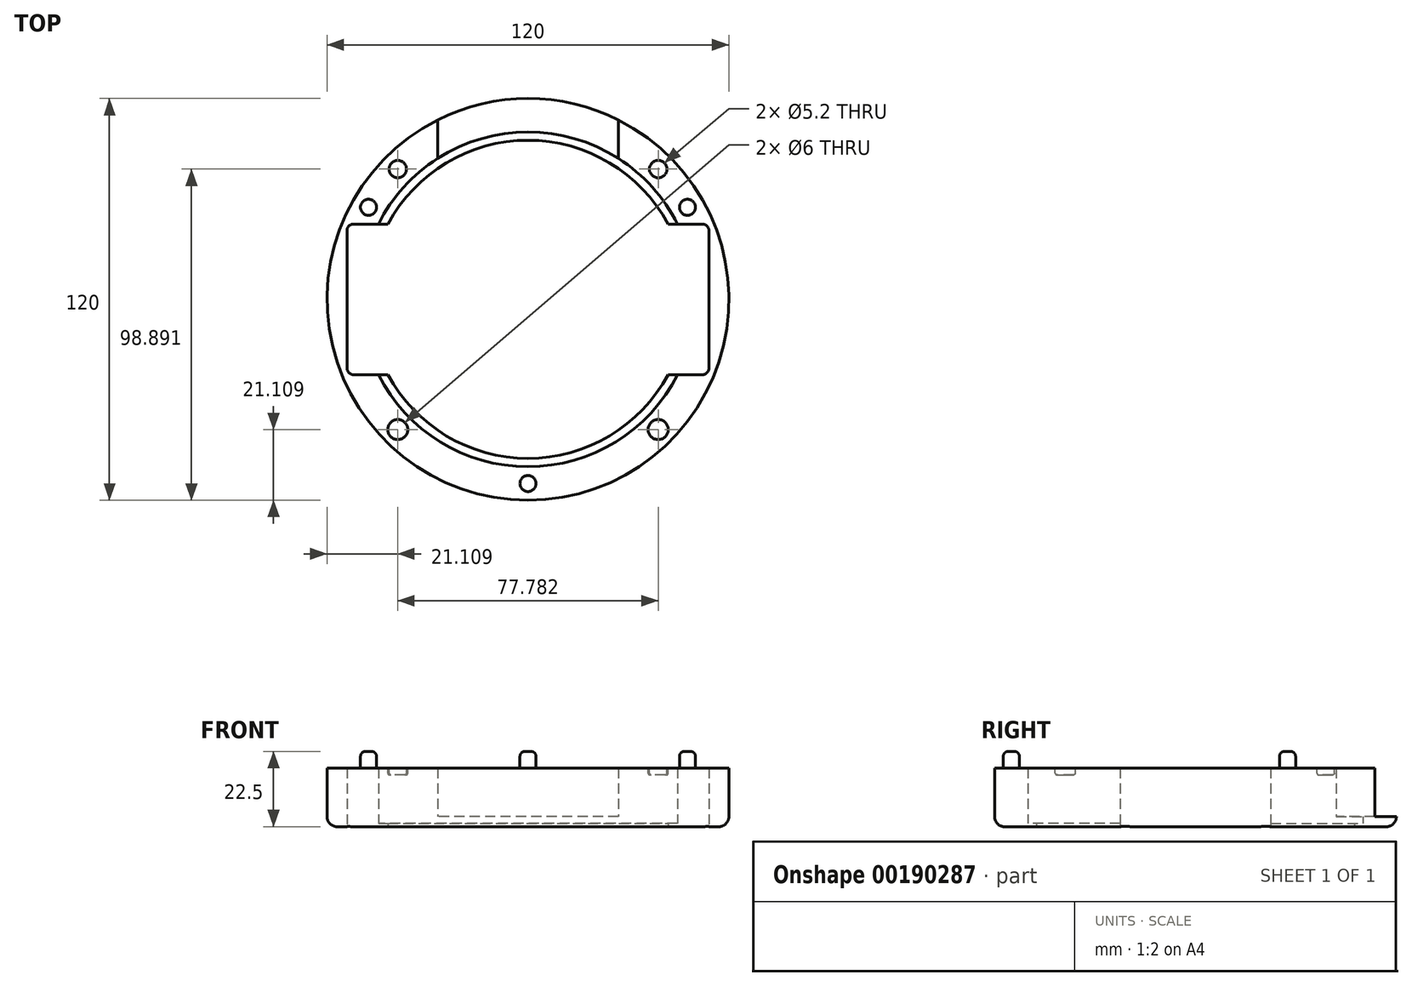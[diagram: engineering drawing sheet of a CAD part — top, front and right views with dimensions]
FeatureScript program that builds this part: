
annotation { "Feature Type Name" : "Feature", "Feature Type Description" : "" }
export const myFeature = defineFeature(function(context is Context, id is Id, definition is map)
    precondition{}
    {
        {
            var Q0;
            Q0=qCreatedBy(makeId("Top.planeOp"),FACE);
            var sketch = newSketch(context, id + "F0", { "sketchPlane" : qUnion([Q0])});
            skCircle(sketch, "E0", {"center": v(0, 0) * mm, "radius": 60 * mm});
            skLineSegment(sketch, "E1", {"start": v(0, 50) * mm, "end": v(0, 50) * mm});
            skArc(sketch, "E2", {"start": v(-44.65, -22.5) * mm, "mid": v(0, -50) * mm, "end": v(44.65, -22.5) * mm});
            skArc(sketch, "E3", {"start": v(-41.83, -22.5) * mm, "mid": v(0, -47.5) * mm, "end": v(41.83, -22.5) * mm});
            skPoint(sketch, "E4.orphan", {"position": v(55.62, -22.5) * mm});
            skLineSegment(sketch, "E5", {"start": v(-44.65, 22.5) * mm, "end": v(-41.83, 22.5) * mm});
            skLineSegment(sketch, "E6", {"start": v(44.65, 22.5) * mm, "end": v(41.83, 22.5) * mm});
            skLineSegment(sketch, "E7.MirrorCS", {"start": v(-44.65, -22.5) * mm, "end": v(-41.83, -22.5) * mm});
            skLineSegment(sketch, "E8.MirrorCS", {"start": v(44.65, -22.5) * mm, "end": v(41.83, -22.5) * mm});
            skArc(sketch, "E9.trimOffspring", {"start": v(41.83, 22.5) * mm, "mid": v(0, 47.5) * mm, "end": v(-41.83, 22.5) * mm});
            skArc(sketch, "E10.trimOffspring", {"start": v(44.65, 22.5) * mm, "mid": v(0, 50) * mm, "end": v(-44.65, 22.5) * mm});
            skLineSegment(sketch, "E11", {"start": v(-27, 53.58) * mm, "end": v(-27, 42.08) * mm});
            skLineSegment(sketch, "E12", {"start": v(27, 53.58) * mm, "end": v(27, 42.08) * mm});
            skLineSegment(sketch, "E13", {"start": v(-27, 53.58) * mm, "end": v(27, 53.58) * mm, "construction": true});
            skLineSegment(sketch, "E14", {"start": v(-44.65, 22.5) * mm, "end": v(-54.05, 22.5) * mm});
            skLineSegment(sketch, "E15", {"start": v(-54.05, 22.5) * mm, "end": v(-54.05, -22.5) * mm});
            skLineSegment(sketch, "E16", {"start": v(-54.05, -22.5) * mm, "end": v(-44.65, -22.5) * mm});
            skLineSegment(sketch, "E17", {"start": v(0, 60) * mm, "end": v(0, -60) * mm, "construction": true});
            skPoint(sketch, "E17.startSnap0", {"position": v(0, 53.58) * mm});
            skPoint(sketch, "E17.endSnap0", {"position": v(0, 47.5) * mm});
            skLineSegment(sketch, "E18.MirrorCS", {"start": v(54.05, 22.5) * mm, "end": v(54.05, -22.5) * mm});
            skLineSegment(sketch, "E19.MirrorCS", {"start": v(44.65, 22.5) * mm, "end": v(54.05, 22.5) * mm});
            skLineSegment(sketch, "E20.MirrorCS", {"start": v(54.05, -22.5) * mm, "end": v(44.65, -22.5) * mm});
            skSolve(sketch);
        }
        {
            var Q0;
            Q0=makeQuery(id+"F0.imprint","IMPRINT",FACE,{"disambiguationData":[TD([[makeQuery(id+"F0.imprint","IMPRINT",EDGE,{"derivedFrom":sQuery(id+"F0.wireOp",EDGE,"E2")}),-1.0]])]});
            extrude(context, id + "F1", {"entities" : qUnion([Q0]), "depth" : 17.5 * mm});
        }
        {
            var Q0;
            Q0=makeQuery(id+"F1.opExtrude","CAP_FACE",FACE,{"disambiguationData":[OSD([sQuery(id+"F0.wireOp",EDGE,"E0"),sQuery(id+"F0.wireOp",EDGE,"E1")])],"isStart":false});
            var sketch = newSketch(context, id + "F2", { "sketchPlane" : qUnion([Q0])});
            skPoint(sketch, "E21.middle", {"position": v(0, 0) * mm});
            skCircle(sketch, "E22", {"center": v(-38.9, 38.9) * mm, "radius": 2.6 * mm});
            skCircle(sketch, "E23", {"center": v(-38.9, -38.9) * mm, "radius": 3 * mm});
            skCircle(sketch, "E24", {"center": v(38.9, -38.9) * mm, "radius": 3 * mm});
            skCircle(sketch, "E25", {"center": v(38.9, 38.9) * mm, "radius": 2.6 * mm});
            skCircle(sketch, "E26", {"center": v(0, -55) * mm, "radius": 2.4 * mm});
            skCircle(sketch, "E27.1.0", {"center": v(47.63, 27.5) * mm, "radius": 2.4 * mm});
            skCircle(sketch, "E27.2.0", {"center": v(-47.63, 27.5) * mm, "radius": 2.4 * mm});
            skSolve(sketch);
        }
        {
            var Q0;
            Q0=makeQuery(id+"F2.imprint","IMPRINT",FACE,{"disambiguationData":[TD([[makeQuery(id+"F2.imprint","IMPRINT",EDGE,{"derivedFrom":sQuery(id+"F2.wireOp",EDGE,"E22")}),1.0]])]});
            var Q1;
            Q1=makeQuery(id+"F2.imprint","IMPRINT",FACE,{"disambiguationData":[TD([[makeQuery(id+"F2.imprint","IMPRINT",EDGE,{"derivedFrom":sQuery(id+"F2.wireOp",EDGE,"E25")}),1.0]])]});
            var Q2;
            Q2=makeQuery(id+"F2.imprint","IMPRINT",FACE,{"disambiguationData":[TD([[makeQuery(id+"F2.imprint","IMPRINT",EDGE,{"derivedFrom":sQuery(id+"F2.wireOp",EDGE,"E24")}),1.0]])]});
            var Q3;
            Q3=makeQuery(id+"F2.imprint","IMPRINT",FACE,{"disambiguationData":[TD([[makeQuery(id+"F2.imprint","IMPRINT",EDGE,{"derivedFrom":sQuery(id+"F2.wireOp",EDGE,"E23")}),1.0]])]});
            extrude(context, id + "F3", {"entities" : qUnion([Q0, Q1, Q2, Q3]), "operationType" : NewBodyOperationType.REMOVE, "oppositeDirection" : true, "depth" : 2 * mm});
        }
        {
            var Q0;
            Q0=makeQuery(id+"F2.imprint","IMPRINT",FACE,{"disambiguationData":[TD([[makeQuery(id+"F2.imprint","IMPRINT",EDGE,{"derivedFrom":sQuery(id+"F2.wireOp",EDGE,"E26")}),1.0]])]});
            var Q1;
            Q1=makeQuery(id+"F2.imprint","IMPRINT",FACE,{"disambiguationData":[TD([[makeQuery(id+"F2.imprint","IMPRINT",EDGE,{"derivedFrom":sQuery(id+"F2.wireOp",EDGE,"E27.1.0")}),1.0]])]});
            var Q2;
            Q2=makeQuery(id+"F2.imprint","IMPRINT",FACE,{"disambiguationData":[TD([[makeQuery(id+"F2.imprint","IMPRINT",EDGE,{"derivedFrom":sQuery(id+"F2.wireOp",EDGE,"E27.2.0")}),1.0]])]});
            var Q3;
            Q3=sQuery(id+"F2.wireOp",EDGE,"VWXdR3C8-mcWa-IJBR-1boV-t68bjsxYqndP");
            var Q4;
            Q4=sQuery(id+"F2.wireOp",EDGE,"uHltdg73-JYHf-iSAY-R7Fn-2nbyHwWvfhgZ");
            var Q5;
            Q5=sQuery(id+"F2.wireOp",EDGE,"R24LEf0a-MQ1t-eLEK-fKfR-x5qMptQUL0lt");
            extrude(context, id + "F4", {"entities" : qUnion([Q0, Q1, Q2]), "operationType" : NewBodyOperationType.ADD, "surfaceEntities" : qUnion([Q3, Q4, Q5]), "depth" : 5 * mm});
        }
        {
            var Q0;
            Q0=makeQuery(id+"F3.boolean.opBoolean","COPY",EDGE,{"derivedFrom":makeQuery(id+"F3.opExtrude","CAP_EDGE",EDGE,{"disambiguationData":[OSD([sQuery(id+"F2.wireOp",EDGE,"E24")])],"isStart":false})});
            var Q1;
            Q1=makeQuery(id+"F3.boolean.opBoolean","COPY",EDGE,{"derivedFrom":makeQuery(id+"F3.opExtrude","CAP_EDGE",EDGE,{"disambiguationData":[OSD([sQuery(id+"F2.wireOp",EDGE,"E23")])],"isStart":false})});
            var Q2;
            Q2=makeQuery(id+"F3.boolean.opBoolean","COPY",EDGE,{"derivedFrom":makeQuery(id+"F3.opExtrude","CAP_EDGE",EDGE,{"disambiguationData":[OSD([sQuery(id+"F2.wireOp",EDGE,"E22")])],"isStart":false})});
            var Q3;
            Q3=makeQuery(id+"F3.boolean.opBoolean","COPY",EDGE,{"derivedFrom":makeQuery(id+"F3.opExtrude","CAP_EDGE",EDGE,{"disambiguationData":[OSD([sQuery(id+"F2.wireOp",EDGE,"E25")])],"isStart":false})});
            fillet(context, id + "F5", {"entities" : qUnion([Q0, Q1, Q2, Q3]), "radius" : 0.5 * mm, "tangentPropagation" : true, "allowEdgeOverflow" : false});
        }
        {
            var Q0;
            Q0=makeQuery(id+"F4.opExtrude","CAP_EDGE",EDGE,{"disambiguationData":[OSD([sQuery(id+"F2.wireOp",EDGE,"E26")])],"isStart":false});
            var Q1;
            Q1=makeQuery(id+"F4.opExtrude","CAP_EDGE",EDGE,{"disambiguationData":[OSD([sQuery(id+"F2.wireOp",EDGE,"E27.2.0")])],"isStart":false});
            var Q2;
            Q2=makeQuery(id+"F4.opExtrude","CAP_EDGE",EDGE,{"disambiguationData":[OSD([sQuery(id+"F2.wireOp",EDGE,"E27.1.0")])],"isStart":false});
            var Q3;
            Q3=makeQuery(id+"FGFiXdv48eJCvJ8_2.boolean.opBoolean","COPY",EDGE,{"derivedFrom":makeQuery(id+"FGFiXdv48eJCvJ8_2.opExtrude","CAP_EDGE",EDGE,{"disambiguationData":[OSD([sQuery(id+"Fr2hoOnM7MHRwgI_2.wireOp",EDGE,"7669c31a-f0c1-4fce-9309-ce77d950d35b.0")])],"isStart":false})});
            var Q4;
            Q4=makeQuery(id+"FGFiXdv48eJCvJ8_2.boolean.opBoolean","COPY",EDGE,{"derivedFrom":makeQuery(id+"FGFiXdv48eJCvJ8_2.opExtrude","CAP_EDGE",EDGE,{"disambiguationData":[OSD([sQuery(id+"Fr2hoOnM7MHRwgI_2.wireOp",EDGE,"7669c31a-f0c1-4fce-9309-ce77d950d35b.1")])],"isStart":false})});
            var Q5;
            Q5=makeQuery(id+"FGFiXdv48eJCvJ8_2.boolean.opBoolean","COPY",EDGE,{"derivedFrom":makeQuery(id+"FGFiXdv48eJCvJ8_2.opExtrude","CAP_EDGE",EDGE,{"disambiguationData":[OSD([sQuery(id+"Fr2hoOnM7MHRwgI_2.wireOp",EDGE,"7669c31a-f0c1-4fce-9309-ce77d950d35b.2")])],"isStart":false})});
            fillet(context, id + "F6", {"entities" : qUnion([Q0, Q1, Q2, Q3, Q4, Q5]), "radius" : 1.5 * mm, "tangentPropagation" : true, "allowEdgeOverflow" : false});
        }
        {
            var Q0;
            Q0=makeQuery(id+"F1.opExtrude","SWEPT_BODY",BODY,{"disambiguationData":[OSD([sQuery(id+"F0.wireOp",EDGE,"E0"),sQuery(id+"F0.wireOp",EDGE,"E1"),sQuery(id+"F0.wireOp",EDGE,"Z948ch8O-qMHw-9Xcc-9FHW-eBQYffAlLzsf"),sQuery(id+"F0.wireOp",EDGE,"A77KNi0v-6heQ-Jye2-6KwH-JstxTwlQuu4X.top"),sQuery(id+"F0.wireOp",EDGE,"A77KNi0v-6heQ-Jye2-6KwH-JstxTwlQuu4X.left"),sQuery(id+"F0.wireOp",EDGE,"A77KNi0v-6heQ-Jye2-6KwH-JstxTwlQuu4X.right"),sQuery(id+"F0.wireOp",EDGE,"e3c13985-3201-4729-a912-cdfdbae41750.trimOffspring"),sQuery(id+"F0.wireOp",EDGE,"hgyFUOab-B19C-UYkE-toPB-BuUCfqlj2oRy.bottom")])]});
            transform(context, id + "F7", {"entities" : qUnion([Q0]), "transformType" : TransformType.TRANSLATION_3D, "dx" : 0 * mm, "dy" : 0 * mm, "dz" : 0 * mm, "makeCopy" : true});
        }
        {
            var Q0;
            Q0=makeQuery(id+"F7.opPattern","COPY",BODY,{"derivedFrom":makeQuery(id+"F1.opExtrude","SWEPT_BODY",BODY,{"disambiguationData":[OSD([sQuery(id+"F0.wireOp",EDGE,"E0"),sQuery(id+"F0.wireOp",EDGE,"E1"),sQuery(id+"F0.wireOp",EDGE,"Z948ch8O-qMHw-9Xcc-9FHW-eBQYffAlLzsf"),sQuery(id+"F0.wireOp",EDGE,"A77KNi0v-6heQ-Jye2-6KwH-JstxTwlQuu4X.top"),sQuery(id+"F0.wireOp",EDGE,"A77KNi0v-6heQ-Jye2-6KwH-JstxTwlQuu4X.left"),sQuery(id+"F0.wireOp",EDGE,"A77KNi0v-6heQ-Jye2-6KwH-JstxTwlQuu4X.right"),sQuery(id+"F0.wireOp",EDGE,"e3c13985-3201-4729-a912-cdfdbae41750.trimOffspring"),sQuery(id+"F0.wireOp",EDGE,"hgyFUOab-B19C-UYkE-toPB-BuUCfqlj2oRy.bottom")])]}),"instanceName":"1"});
            deleteBodies(context, id + "F8", {"entities" : qUnion([Q0])});
        }
        {
            var Q0;
            Q0=makeQuery(id+"F0.imprint","IMPRINT",FACE,{"disambiguationData":[TD([[makeQuery(id+"F0.imprint","IMPRINT",EDGE,{"derivedFrom":sQuery(id+"F0.wireOp",EDGE,"E2")}),1.0]])]});
            var sketch = newSketch(context, id + "F9", { "sketchPlane" : qUnion([Q0])});
            skSolve(sketch);
        }
        {
            var Q0;
            Q0 = qSketchRegion(id + "F9", true);
            var Q1;
            Q1=makeQuery(id+"F0.imprint","IMPRINT",FACE,{"disambiguationData":[TD([[makeQuery(id+"F0.imprint","IMPRINT",EDGE,{"derivedFrom":sQuery(id+"F0.wireOp",EDGE,"E2")}),1.0]])]});
            var Q2;
            Q2=makeQuery(id+"F0.imprint","IMPRINT",FACE,{"disambiguationData":[TD([[makeQuery(id+"F0.imprint","IMPRINT",EDGE,{"derivedFrom":sQuery(id+"F0.wireOp",EDGE,"E5")}),1.0]])]});
            extrude(context, id + "F10", {"entities" : qUnion([Q0, Q1, Q2]), "operationType" : NewBodyOperationType.ADD, "depth" : 1 * mm});
        }
        {
            var Q0;
            {var subQ0=sQuery(id+"F0.wireOp",EDGE,"E11");Q0=makeQuery(id+"F0.imprint","IMPRINT",FACE,{"disambiguationData":[TD([[makeQuery(id+"F0.imprint","IMPRINT",EDGE,{"derivedFrom":subQ0}),1.0]])]});}
            extrude(context, id + "F11", {"entities" : qUnion([Q0]), "operationType" : NewBodyOperationType.ADD, "depth" : 3 * mm});
        }
        {
            var Q0;
            Q0=makeQuery(id+"F1.opExtrude","SWEPT_EDGE",EDGE,{"disambiguationData":[OSD([sQuery(id+"F0.wireOp",EDGE,"E14"),sQuery(id+"F0.wireOp",EDGE,"E15")])]});
            var Q1;
            Q1=makeQuery(id+"F1.opExtrude","SWEPT_EDGE",EDGE,{"disambiguationData":[OSD([sQuery(id+"F0.wireOp",EDGE,"E18.MirrorCS"),sQuery(id+"F0.wireOp",EDGE,"E19.MirrorCS")])]});
            var Q2;
            Q2=makeQuery(id+"F1.opExtrude","SWEPT_EDGE",EDGE,{"disambiguationData":[OSD([sQuery(id+"F0.wireOp",EDGE,"E18.MirrorCS"),sQuery(id+"F0.wireOp",EDGE,"E20.MirrorCS")])]});
            var Q3;
            Q3=makeQuery(id+"F1.opExtrude","SWEPT_EDGE",EDGE,{"disambiguationData":[OSD([sQuery(id+"F0.wireOp",EDGE,"E15"),sQuery(id+"F0.wireOp",EDGE,"E16")])]});
            fillet(context, id + "F12", {"entities" : qUnion([Q0, Q1, Q2, Q3]), "radius" : 2 * mm, "tangentPropagation" : true, "allowEdgeOverflow" : false});
        }
        {
            var Q0;
            {var subQ0=sQuery(id+"F0.wireOp",EDGE,"E0");Q0=makeQuery(id+"F11.boolean.opBoolean","MERGE",EDGE,{"derivedFrom":[makeQuery(id+"F1.opExtrude","CAP_EDGE",EDGE,{"disambiguationData":[OSD([subQ0])],"isStart":true}),makeQuery(id+"F11.opExtrude","CAP_EDGE",EDGE,{"disambiguationData":[OSD([subQ0])],"isStart":true})]});}
            fillet(context, id + "F13", {"entities" : qUnion([Q0]), "radius" : 3 * mm, "tangentPropagation" : true, "allowEdgeOverflow" : false});
        }
    });
